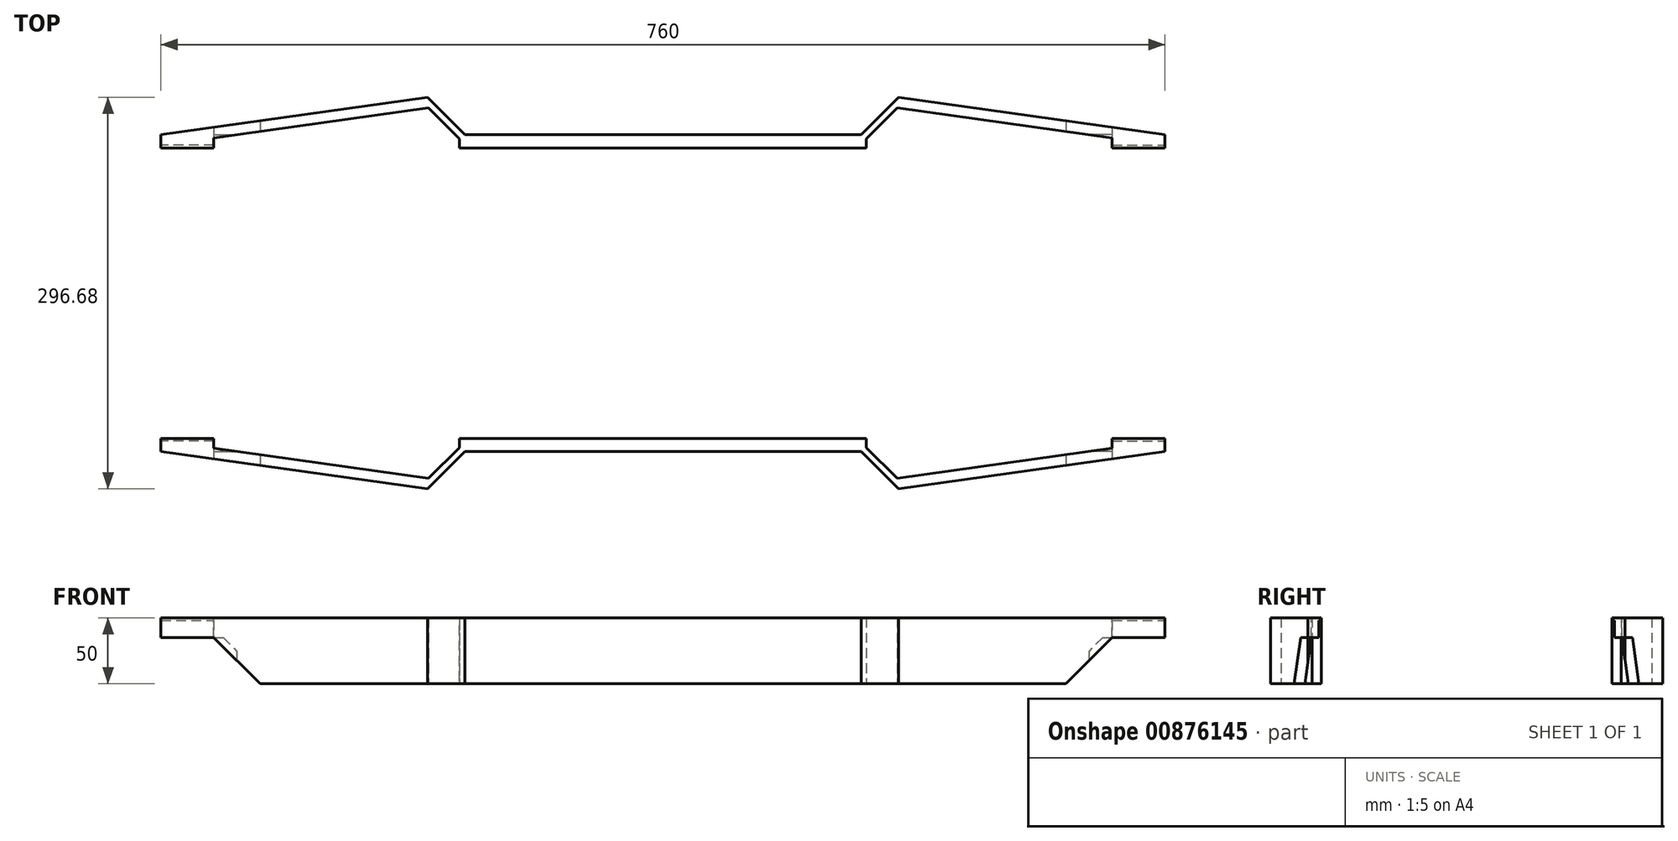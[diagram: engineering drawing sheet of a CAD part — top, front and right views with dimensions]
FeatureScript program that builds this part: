
annotation { "Feature Type Name" : "Feature", "Feature Type Description" : "" }
export const myFeature = defineFeature(function(context is Context, id is Id, definition is map)
    precondition{}
    {
        {
            var Q0;
            Q0=qCreatedBy(makeId("Top.planeOp"),FACE);
            var sketch = newSketch(context, id + "F0", { "sketchPlane" : qUnion([Q0])});
            skLineSegment(sketch, "E0", {"start": v(-380, 120) * mm, "end": v(-380, -120) * mm});
            skLineSegment(sketch, "E1", {"start": v(380, 120) * mm, "end": v(380, -120) * mm});
            skLineSegment(sketch, "E2", {"start": v(150, -120) * mm, "end": v(-150, -120) * mm});
            skLineSegment(sketch, "E3", {"start": v(-150, 120) * mm, "end": v(150, 120) * mm});
            skLineSegment(sketch, "E4", {"start": v(-160, 110) * mm, "end": v(160, 110) * mm, "construction": true});
            skLineSegment(sketch, "E5", {"start": v(160, 110) * mm, "end": v(160, -110) * mm, "construction": true});
            skLineSegment(sketch, "E6", {"start": v(160, -110) * mm, "end": v(-160, -110) * mm, "construction": true});
            skLineSegment(sketch, "E7", {"start": v(-160, -110) * mm, "end": v(-160, 110) * mm, "construction": true});
            skLineSegment(sketch, "E8.0", {"start": v(-150, -110) * mm, "end": v(-150, 110) * mm, "construction": true});
            skLineSegment(sketch, "E9.0", {"start": v(150, 110) * mm, "end": v(150, -110) * mm, "construction": true});
            skLineSegment(sketch, "E10", {"start": v(-150, -110) * mm, "end": v(-150, -120) * mm, "construction": true});
            skLineSegment(sketch, "E11", {"start": v(-150, 110) * mm, "end": v(-150, 120) * mm, "construction": true});
            skLineSegment(sketch, "E12", {"start": v(-150, 120) * mm, "end": v(-178.34, 148.34) * mm});
            skLineSegment(sketch, "E13", {"start": v(-380, 120) * mm, "end": v(-178.34, 148.34) * mm});
            skPoint(sketch, "E14.endSnap0", {"position": v(0, 110) * mm});
            skLineSegment(sketch, "E15.MirrorCS", {"start": v(150, 120) * mm, "end": v(178.34, 148.34) * mm});
            skLineSegment(sketch, "E16.MirrorCS", {"start": v(380, 120) * mm, "end": v(178.34, 148.34) * mm});
            skLineSegment(sketch, "E17.MirrorCS", {"start": v(-150, -120) * mm, "end": v(-178.34, -148.34) * mm, "construction": true});
            skLineSegment(sketch, "E18.MirrorCS", {"start": v(-380, -120) * mm, "end": v(-178.34, -148.34) * mm});
            skLineSegment(sketch, "E19.MirrorCS", {"start": v(150, -120) * mm, "end": v(178.34, -148.34) * mm});
            skLineSegment(sketch, "E20.MirrorCS", {"start": v(-150, -120) * mm, "end": v(-178.34, -148.34) * mm});
            skLineSegment(sketch, "E21.MirrorCS", {"start": v(380, -120) * mm, "end": v(178.34, -148.34) * mm});
            skSolve(sketch);
        }
        {
            var Q0;
            Q0=makeQuery(id+"F0.imprint","IMPRINT",FACE,{"disambiguationData":[TD([[makeQuery(id+"F0.imprint","IMPRINT",EDGE,{"derivedFrom":sQuery(id+"F0.wireOp",EDGE,"E0")}),1.0]])]});
            extrude(context, id + "F1", {"entities" : qUnion([Q0]), "depth" : 50 * mm, "offsetDistance" : 25 * mm});
        }
        {
            var Q0;
            Q0=makeQuery(id+"F1.opExtrude","SWEPT_FACE",FACE,{"disambiguationData":[OSD([sQuery(id+"F0.wireOp",EDGE,"E2")])]});
            var sketch = newSketch(context, id + "F2", { "sketchPlane" : qUnion([Q0])});
            skLineSegment(sketch, "E22", {"start": v(-380, 35) * mm, "end": v(-340, 35) * mm});
            skLineSegment(sketch, "E23", {"start": v(-340, 35) * mm, "end": v(-305, 0) * mm});
            skLineSegment(sketch, "E24", {"start": v(-380, 35) * mm, "end": v(-380, 0) * mm});
            skLineSegment(sketch, "E25", {"start": v(-380, 0) * mm, "end": v(-305, 0) * mm});
            skLineSegment(sketch, "E26.MirrorCS", {"start": v(380, 0) * mm, "end": v(305, 0) * mm});
            skLineSegment(sketch, "E27.MirrorCS", {"start": v(380, 35) * mm, "end": v(380, 0) * mm});
            skLineSegment(sketch, "E28.MirrorCS", {"start": v(380, 35) * mm, "end": v(340, 35) * mm});
            skLineSegment(sketch, "E29.MirrorCS", {"start": v(340, 35) * mm, "end": v(305, 0) * mm});
            skSolve(sketch);
        }
        {
            var Q0;
            Q0=makeQuery(id+"F1.opExtrude","SWEPT_FACE",FACE,{"disambiguationData":[OSD([sQuery(id+"F0.wireOp",EDGE,"E0")])]});
            var sketch = newSketch(context, id + "F3", { "sketchPlane" : qUnion([Q0])});
            skLineSegment(sketch, "E30.0", {"start": v(-110, 45) * mm, "end": v(110, 45) * mm});
            skLineSegment(sketch, "E31.0", {"start": v(-110, 5) * mm, "end": v(110, 5) * mm});
            skLineSegment(sketch, "E32.0", {"start": v(-110, 5) * mm, "end": v(-110, 45) * mm});
            skLineSegment(sketch, "E33.0", {"start": v(110, 45) * mm, "end": v(110, 5) * mm});
            skSolve(sketch);
        }
        {
            var Q0;
            Q0=makeQuery(id+"F3.imprint","IMPRINT",FACE,{"disambiguationData":[TD([[makeQuery(id+"F3.imprint","IMPRINT",EDGE,{"derivedFrom":sQuery(id+"F3.wireOp",EDGE,"E30.0")}),-1.0]])]});
            extrude(context, id + "F4", {"entities" : qUnion([Q0]), "operationType" : NewBodyOperationType.REMOVE, "oppositeDirection" : true, "depth" : 760 * mm, "offsetDistance" : 25 * mm});
        }
        {
            var Q0;
            Q0=makeQuery(id+"F2.imprint","IMPRINT",FACE,{"disambiguationData":[TD([[makeQuery(id+"F2.imprint","IMPRINT",EDGE,{"derivedFrom":sQuery(id+"F2.wireOp",EDGE,"E26.MirrorCS")}),-1.0]])]});
            var Q1;
            Q1=makeQuery(id+"F2.imprint","IMPRINT",FACE,{"disambiguationData":[TD([[makeQuery(id+"F2.imprint","IMPRINT",EDGE,{"derivedFrom":sQuery(id+"F2.wireOp",EDGE,"E22")}),-1.0]])]});
            extrude(context, id + "F5", {"entities" : qUnion([Q0, Q1]), "operationType" : NewBodyOperationType.REMOVE, "oppositeDirection" : true, "depth" : 240 * mm, "offsetDistance" : 25 * mm});
        }
        {
            var Q0;
            Q0=makeQuery(id+"F1.opExtrude","CAP_FACE",FACE,{"disambiguationData":[OSD([sQuery(id+"F0.wireOp",EDGE,"E0"),sQuery(id+"F0.wireOp",EDGE,"E1"),sQuery(id+"F0.wireOp",EDGE,"E2"),sQuery(id+"F0.wireOp",EDGE,"E3")])],"isStart":false});
            var sketch = newSketch(context, id + "F6", { "sketchPlane" : qUnion([Q0])});
            skLineSegment(sketch, "E34", {"start": v(-140, 90) * mm, "end": v(140, 90) * mm});
            skLineSegment(sketch, "E35", {"start": v(140, 90) * mm, "end": v(140, -90) * mm});
            skLineSegment(sketch, "E36", {"start": v(140, -90) * mm, "end": v(-140, -90) * mm});
            skLineSegment(sketch, "E37", {"start": v(-140, -90) * mm, "end": v(-140, 90) * mm});
            skLineSegment(sketch, "E38", {"start": v(160, 110) * mm, "end": v(160, -110) * mm});
            skLineSegment(sketch, "E39", {"start": v(-160, 110) * mm, "end": v(-160, -110) * mm});
            skLineSegment(sketch, "E40", {"start": v(-160, 110) * mm, "end": v(160, 110) * mm});
            skLineSegment(sketch, "E41", {"start": v(160, -110) * mm, "end": v(-160, -110) * mm});
            skSolve(sketch);
        }
        {
            var Q0;
            Q0=qSketchRegion(id+"F6",true);
            extrude(context, id + "F7", {"entities" : qUnion([Q0]), "operationType" : NewBodyOperationType.REMOVE, "oppositeDirection" : true, "depth" : 50 * mm, "offsetDistance" : 25 * mm});
        }
        {
            var Q0;
            Q0=qSketchRegion(id+"F2",true);
            extrude(context, id + "F8", {"entities" : qUnion([Q0]), "operationType" : NewBodyOperationType.REMOVE, "endBound" : BoundingType.SYMMETRIC, "oppositeDirection" : true, "depth" : 871.86 * mm, "offsetDistance" : 25 * mm});
        }
        {
            var Q0;
            {var subQ0=sQuery(id+"F0.wireOp",EDGE,"E18.MirrorCS");var subQ1=sQuery(id+"F0.wireOp",EDGE,"E16.MirrorCS");var subQ2=sQuery(id+"F0.wireOp",EDGE,"E15.MirrorCS");var subQ3=sQuery(id+"F0.wireOp",EDGE,"E13");var subQ4=sQuery(id+"F0.wireOp",EDGE,"E12");var subQ5=sQuery(id+"F0.wireOp",EDGE,"E19.MirrorCS");var subQ6=sQuery(id+"F0.wireOp",EDGE,"E0");var subQ7=sQuery(id+"F0.wireOp",EDGE,"E3");var subQ8=sQuery(id+"F0.wireOp",EDGE,"E1");var subQ9=sQuery(id+"F0.wireOp",EDGE,"E2");var subQ10=sQuery(id+"F0.wireOp",EDGE,"E20.MirrorCS");var subQ11=sQuery(id+"F0.wireOp",EDGE,"E21.MirrorCS");Q0=makeQuery(id+"F7.boolean.opBoolean","SPLIT",FACE,{"disambiguationData":[TD([makeQuery(id+"F1.opExtrude","SWEPT_FACE",FACE,{"disambiguationData":[OSD([subQ6])]})])],"derivedFrom":makeQuery(id+"F1.opExtrude","CAP_FACE",FACE,{"disambiguationData":[OSD([subQ6,subQ8,subQ9,subQ7,subQ4,subQ3,subQ2,subQ1,subQ0,subQ5,subQ10,subQ11])],"isStart":false})});}
            var sketch = newSketch(context, id + "F9", { "sketchPlane" : qUnion([Q0])});
            skLineSegment(sketch, "E42", {"start": v(-165, -110) * mm, "end": v(-305, -110) * mm});
            skLineSegment(sketch, "E43", {"start": v(-305, -110) * mm, "end": v(-305, 110) * mm});
            skLineSegment(sketch, "E44", {"start": v(-305, 110) * mm, "end": v(-165, 110) * mm});
            skLineSegment(sketch, "E45.0", {"start": v(-165, 110) * mm, "end": v(-165, -110) * mm});
            skLineSegment(sketch, "E46", {"start": v(0, 0) * mm, "end": v(0, 58.76) * mm});
            skLineSegment(sketch, "E47.MirrorCS", {"start": v(165, 110) * mm, "end": v(165, -110) * mm});
            skLineSegment(sketch, "E48.MirrorCS", {"start": v(165, -110) * mm, "end": v(305, -110) * mm});
            skLineSegment(sketch, "E49.MirrorCS", {"start": v(305, -110) * mm, "end": v(305, 110) * mm});
            skLineSegment(sketch, "E50.MirrorCS", {"start": v(305, 110) * mm, "end": v(165, 110) * mm});
            skSolve(sketch);
        }
        {
            var Q0;
            Q0=makeQuery(id+"F9.imprint","IMPRINT",FACE,{"disambiguationData":[TD([[makeQuery(id+"F9.imprint","IMPRINT",EDGE,{"derivedFrom":sQuery(id+"F9.wireOp",EDGE,"E42")}),-1.0]])]});
            var Q1;
            Q1=makeQuery(id+"F9.imprint","IMPRINT",FACE,{"disambiguationData":[TD([[makeQuery(id+"F9.imprint","IMPRINT",EDGE,{"derivedFrom":sQuery(id+"F9.wireOp",EDGE,"E47.MirrorCS")}),1.0]])]});
            extrude(context, id + "F10", {"entities" : qUnion([Q0, Q1]), "operationType" : NewBodyOperationType.REMOVE, "oppositeDirection" : true, "depth" : 10 * mm, "offsetDistance" : 25 * mm});
        }
        {
            var Q0;
            Q0=makeQuery(id+"F1.opExtrude","SWEPT_FACE",FACE,{"disambiguationData":[OSD([sQuery(id+"F0.wireOp",EDGE,"E2")])]});
            var sketch = newSketch(context, id + "F11", { "sketchPlane" : qUnion([Q0])});
            skLineSegment(sketch, "E51", {"start": v(-305, 50) * mm, "end": v(-305, 0) * mm});
            skLineSegment(sketch, "E52", {"start": v(-340, 50) * mm, "end": v(-340, 35) * mm});
            skLineSegment(sketch, "E53", {"start": v(-340, 35) * mm, "end": v(-305, 0) * mm});
            skLineSegment(sketch, "E54.0", {"start": v(-332.93, 35) * mm, "end": v(-305, 7.07) * mm});
            skLineSegment(sketch, "E55", {"start": v(-340, 35) * mm, "end": v(-332.93, 35) * mm});
            skLineSegment(sketch, "E56", {"start": v(0, 0) * mm, "end": v(0, 50) * mm});
            skLineSegment(sketch, "E57", {"start": v(-340, 35) * mm, "end": v(-346.55, 35) * mm});
            skLineSegment(sketch, "E58.MirrorCS", {"start": v(332.93, 35) * mm, "end": v(305, 7.07) * mm});
            skLineSegment(sketch, "E59.MirrorCS", {"start": v(340, 35) * mm, "end": v(305, 0) * mm});
            skLineSegment(sketch, "E60.MirrorCS", {"start": v(340, 35) * mm, "end": v(332.93, 35) * mm});
            skLineSegment(sketch, "E61", {"start": v(305, 7.07) * mm, "end": v(305, 0) * mm});
            skSolve(sketch);
        }
        {
            var Q0;
            {var subQ0=sQuery(id+"F11.wireOp",EDGE,"E53");Q0=makeQuery(id+"F11.imprint","IMPRINT",FACE,{"disambiguationData":[TD([[makeQuery(id+"F11.imprint","IMPRINT",EDGE,{"derivedFrom":subQ0}),1.0]])]});}
            var Q1;
            Q1=makeQuery(id+"F11.imprint","IMPRINT",FACE,{"disambiguationData":[TD([[makeQuery(id+"F11.imprint","IMPRINT",EDGE,{"derivedFrom":sQuery(id+"F11.wireOp",EDGE,"E58.MirrorCS")}),1.0]])]});
            extrude(context, id + "F12", {"entities" : qUnion([Q0, Q1]), "oppositeDirection" : true, "depth" : 240 * mm, "offsetDistance" : 25 * mm});
        }
        {
            var Q0;
            Q0=makeQuery(id+"F7.boolean.opBoolean","SPLIT",FACE,{"disambiguationData":[TD([makeQuery(id+"F7.opExtrude","SWEPT_FACE",FACE,{"disambiguationData":[OSD([sQuery(id+"F6.wireOp",EDGE,"E34")])]})])],"derivedFrom":makeQuery(id+"F1.opExtrude","CAP_FACE",FACE,{"disambiguationData":[OSD([sQuery(id+"F0.wireOp",EDGE,"E0"),sQuery(id+"F0.wireOp",EDGE,"E1"),sQuery(id+"F0.wireOp",EDGE,"E2"),sQuery(id+"F0.wireOp",EDGE,"E3"),sQuery(id+"F0.wireOp",EDGE,"E12"),sQuery(id+"F0.wireOp",EDGE,"E13"),sQuery(id+"F0.wireOp",EDGE,"E15.MirrorCS"),sQuery(id+"F0.wireOp",EDGE,"E16.MirrorCS"),sQuery(id+"F0.wireOp",EDGE,"E18.MirrorCS"),sQuery(id+"F0.wireOp",EDGE,"E19.MirrorCS"),sQuery(id+"F0.wireOp",EDGE,"E20.MirrorCS"),sQuery(id+"F0.wireOp",EDGE,"E21.MirrorCS")])],"isStart":false})});
            extrude(context, id + "F13", {"entities" : qUnion([Q0]), "operationType" : NewBodyOperationType.REMOVE, "oppositeDirection" : true, "depth" : 25 * mm, "offsetDistance" : 25 * mm});
        }
        {
            var Q0;
            Q0=makeQuery(id+"F7.boolean.opBoolean","SPLIT",FACE,{"disambiguationData":[TD([makeQuery(id+"F7.opExtrude","SWEPT_FACE",FACE,{"disambiguationData":[OSD([sQuery(id+"F6.wireOp",EDGE,"E34")])]})])],"derivedFrom":makeQuery(id+"F1.opExtrude","CAP_FACE",FACE,{"disambiguationData":[OSD([sQuery(id+"F0.wireOp",EDGE,"E0"),sQuery(id+"F0.wireOp",EDGE,"E1"),sQuery(id+"F0.wireOp",EDGE,"E2"),sQuery(id+"F0.wireOp",EDGE,"E3"),sQuery(id+"F0.wireOp",EDGE,"E12"),sQuery(id+"F0.wireOp",EDGE,"E13"),sQuery(id+"F0.wireOp",EDGE,"E15.MirrorCS"),sQuery(id+"F0.wireOp",EDGE,"E16.MirrorCS"),sQuery(id+"F0.wireOp",EDGE,"E18.MirrorCS"),sQuery(id+"F0.wireOp",EDGE,"E19.MirrorCS"),sQuery(id+"F0.wireOp",EDGE,"E20.MirrorCS"),sQuery(id+"F0.wireOp",EDGE,"E21.MirrorCS")])],"isStart":true})});
            extrude(context, id + "F14", {"entities" : qUnion([Q0]), "operationType" : NewBodyOperationType.REMOVE, "oppositeDirection" : true, "depth" : 25 * mm, "offsetDistance" : 25 * mm});
        }
        {
            var Q0;
            Q0=makeQuery(id+"F7.boolean.opBoolean","COPY",FACE,{"disambiguationData":[TD([makeQuery(id+"F4.boolean.opBoolean","COPY",FACE,{"derivedFrom":makeQuery(id+"F4.opExtrude","SWEPT_FACE",FACE,{"disambiguationData":[OSD([sQuery(id+"F3.wireOp",EDGE,"E30.0")])]})})])],"derivedFrom":makeQuery(id+"F7.opExtrude","SWEPT_FACE",FACE,{"disambiguationData":[OSD([sQuery(id+"F6.wireOp",EDGE,"E38")])]})});
            var sketch = newSketch(context, id + "F15", { "sketchPlane" : qUnion([Q0])});
            skLineSegment(sketch, "E62", {"start": v(-110, 45) * mm, "end": v(-110, 5) * mm});
            skLineSegment(sketch, "E63", {"start": v(-110, 45) * mm, "end": v(110, 45) * mm});
            skLineSegment(sketch, "E64", {"start": v(110, 45) * mm, "end": v(110, 5) * mm});
            skLineSegment(sketch, "E65", {"start": v(-110, 5) * mm, "end": v(110, 5) * mm});
            skSolve(sketch);
        }
        {
            var Q0;
            Q0=makeQuery(id+"F7.boolean.opBoolean","COPY",FACE,{"disambiguationData":[TD([makeQuery(id+"F4.boolean.opBoolean","COPY",FACE,{"derivedFrom":makeQuery(id+"F4.opExtrude","SWEPT_FACE",FACE,{"disambiguationData":[OSD([sQuery(id+"F3.wireOp",EDGE,"E31.0")])]})})])],"derivedFrom":makeQuery(id+"F7.opExtrude","SWEPT_FACE",FACE,{"disambiguationData":[OSD([sQuery(id+"F6.wireOp",EDGE,"E39")])]})});
            var sketch = newSketch(context, id + "F16", { "sketchPlane" : qUnion([Q0])});
            skLineSegment(sketch, "E66", {"start": v(-110, 5) * mm, "end": v(-110, 45) * mm});
            skLineSegment(sketch, "E67", {"start": v(-110, 5) * mm, "end": v(110, 5) * mm});
            skLineSegment(sketch, "E68", {"start": v(110, 5) * mm, "end": v(110, 45) * mm});
            skLineSegment(sketch, "E69", {"start": v(-110, 45) * mm, "end": v(110, 45) * mm});
            skSolve(sketch);
        }
        {
            var Q0;
            Q0=qSketchRegion(id+"F16",true);
            extrude(context, id + "F17", {"entities" : qUnion([Q0]), "operationType" : NewBodyOperationType.ADD, "oppositeDirection" : true, "depth" : 5 * mm, "offsetDistance" : 25 * mm});
        }
        {
            var Q0;
            Q0=makeQuery(id+"F15.imprint","IMPRINT",FACE,{"disambiguationData":[TD([[makeQuery(id+"F15.imprint","IMPRINT",EDGE,{"derivedFrom":sQuery(id+"F15.wireOp",EDGE,"E62")}),1.0]])]});
            extrude(context, id + "F18", {"entities" : qUnion([Q0]), "operationType" : NewBodyOperationType.ADD, "oppositeDirection" : true, "depth" : 5 * mm, "offsetDistance" : 25 * mm});
        }
        {
            var Q0;
            Q0=makeQuery(id+"F10.boolean.opBoolean","COPY",FACE,{"derivedFrom":makeQuery(id+"F10.opExtrude","SWEPT_FACE",FACE,{"disambiguationData":[OSD([sQuery(id+"F9.wireOp",EDGE,"E43")])]})});
            extrude(context, id + "F19", {"entities" : qUnion([Q0]), "operationType" : NewBodyOperationType.REMOVE, "oppositeDirection" : true, "depth" : 121.6 * mm, "offsetDistance" : 25 * mm});
        }
        {
            var Q0;
            Q0=makeQuery(id+"F10.boolean.opBoolean","COPY",FACE,{"derivedFrom":makeQuery(id+"F10.opExtrude","SWEPT_FACE",FACE,{"disambiguationData":[OSD([sQuery(id+"F9.wireOp",EDGE,"E49.MirrorCS")])]})});
            extrude(context, id + "F20", {"entities" : qUnion([Q0]), "operationType" : NewBodyOperationType.REMOVE, "endBound" : BoundingType.SYMMETRIC, "depth" : 2865.48 * mm, "offsetDistance" : 25 * mm});
        }
        {
            var Q0;
            Q0=makeQuery(id+"F17.boolean.opBoolean","MERGE",FACE,{"derivedFrom":[makeQuery(id+"F10.boolean.opBoolean","COPY",FACE,{"derivedFrom":makeQuery(id+"F10.opExtrude","SWEPT_FACE",FACE,{"disambiguationData":[OSD([sQuery(id+"F9.wireOp",EDGE,"E45.0")])]})}),makeQuery(id+"F17.opExtrude","CAP_FACE",FACE,{"disambiguationData":[OSD([sQuery(id+"F16.wireOp",EDGE,"E66"),sQuery(id+"F16.wireOp",EDGE,"E67"),sQuery(id+"F16.wireOp",EDGE,"E68"),sQuery(id+"F16.wireOp",EDGE,"E69")])],"isStart":false})]});
            extrude(context, id + "F21", {"entities" : qUnion([Q0]), "operationType" : NewBodyOperationType.REMOVE, "endBound" : BoundingType.SYMMETRIC, "oppositeDirection" : true, "depth" : 1589.2 * mm, "offsetDistance" : 25 * mm});
        }
        {
            var Q0;
            {var subQ16=makeQuery(id+"F7.opExtrude","SWEPT_FACE",FACE,{"disambiguationData":[OSD([sQuery(id+"F6.wireOp",EDGE,"E39")])]});Q0=makeQuery(id+"F17.boolean.opBoolean","MERGE",FACE,{"derivedFrom":[makeQuery(id+"F7.boolean.opBoolean","COPY",FACE,{"disambiguationData":[TD([makeQuery(id+"F4.boolean.opBoolean","COPY",FACE,{"derivedFrom":makeQuery(id+"F4.opExtrude","SWEPT_FACE",FACE,{"disambiguationData":[OSD([sQuery(id+"F3.wireOp",EDGE,"E30.0")])]})})])],"derivedFrom":subQ16}),makeQuery(id+"F7.boolean.opBoolean","COPY",FACE,{"disambiguationData":[TD([makeQuery(id+"F4.boolean.opBoolean","COPY",FACE,{"derivedFrom":makeQuery(id+"F4.opExtrude","SWEPT_FACE",FACE,{"disambiguationData":[OSD([sQuery(id+"F3.wireOp",EDGE,"E31.0")])]})})])],"derivedFrom":subQ16}),makeQuery(id+"F17.opExtrude","CAP_FACE",FACE,{"disambiguationData":[OSD([sQuery(id+"F16.wireOp",EDGE,"E66"),sQuery(id+"F16.wireOp",EDGE,"E67"),sQuery(id+"F16.wireOp",EDGE,"E68"),sQuery(id+"F16.wireOp",EDGE,"E69")])],"isStart":true})]});}
            extrude(context, id + "F22", {"entities" : qUnion([Q0]), "operationType" : NewBodyOperationType.REMOVE, "endBound" : BoundingType.SYMMETRIC, "depth" : 1696.6 * mm, "offsetDistance" : 25 * mm});
        }
        {
            var Q0;
            {var subQ1=sQuery(id+"F0.wireOp",EDGE,"E19.MirrorCS");var subQ3=sQuery(id+"F0.wireOp",EDGE,"E21.MirrorCS");var subQ7=sQuery(id+"F0.wireOp",EDGE,"E2");var subQ8=makeQuery(id+"F1.opExtrude","SWEPT_FACE",FACE,{"disambiguationData":[OSD([subQ7])]});var subQ9=sQuery(id+"F0.wireOp",EDGE,"E18.MirrorCS");var subQ13=sQuery(id+"F0.wireOp",EDGE,"E20.MirrorCS");var subQ17=sQuery(id+"F0.wireOp",EDGE,"E16.MirrorCS");var subQ18=sQuery(id+"F0.wireOp",EDGE,"E15.MirrorCS");var subQ22=sQuery(id+"F0.wireOp",EDGE,"E3");var subQ23=sQuery(id+"F0.wireOp",EDGE,"E12");var subQ27=sQuery(id+"F0.wireOp",EDGE,"E13");Q0=makeQuery(id+"F22.boolean.opBoolean","SPLIT",FACE,{"disambiguationData":[TD([subQ8])],"derivedFrom":makeQuery(id+"F7.boolean.opBoolean","SPLIT",FACE,{"disambiguationData":[TD([subQ8])],"derivedFrom":makeQuery(id+"F1.opExtrude","CAP_FACE",FACE,{"disambiguationData":[OSD([sQuery(id+"F0.wireOp",EDGE,"E0"),sQuery(id+"F0.wireOp",EDGE,"E1"),subQ7,subQ22,subQ23,subQ27,subQ18,subQ17,subQ9,subQ1,subQ13,subQ3])],"isStart":true})})});}
            var sketch = newSketch(context, id + "F23", { "sketchPlane" : qUnion([Q0])});
            skLineSegment(sketch, "E70", {"start": v(-301, 110) * mm, "end": v(-154, 110) * mm});
            skLineSegment(sketch, "E71.0", {"start": v(-177.46, 140.39) * mm, "end": v(-301, 123.02) * mm});
            skLineSegment(sketch, "E72.0", {"start": v(-301, 123.02) * mm, "end": v(-301, 110) * mm});
            skLineSegment(sketch, "E73.0", {"start": v(-154, 116.93) * mm, "end": v(-177.46, 140.39) * mm});
            skLineSegment(sketch, "E74.0", {"start": v(-154, 110) * mm, "end": v(-154, 116.93) * mm});
            skLineSegment(sketch, "E75.MirrorCS", {"start": v(-301, -110) * mm, "end": v(-154, -110) * mm});
            skLineSegment(sketch, "E76.MirrorCS", {"start": v(-177.46, -140.39) * mm, "end": v(-301, -123.02) * mm});
            skLineSegment(sketch, "E77.MirrorCS", {"start": v(-301, -123.02) * mm, "end": v(-301, -110) * mm});
            skLineSegment(sketch, "E78.MirrorCS", {"start": v(-154, -116.93) * mm, "end": v(-177.46, -140.39) * mm});
            skLineSegment(sketch, "E79.MirrorCS", {"start": v(-154, -110) * mm, "end": v(-154, -116.93) * mm});
            skLineSegment(sketch, "E80.MirrorCS", {"start": v(154, 116.93) * mm, "end": v(177.46, 140.39) * mm});
            skLineSegment(sketch, "E81.MirrorCS", {"start": v(301, 110) * mm, "end": v(154, 110) * mm});
            skLineSegment(sketch, "E82.MirrorCS", {"start": v(301, -110) * mm, "end": v(154, -110) * mm});
            skLineSegment(sketch, "E83.MirrorCS", {"start": v(154, 110) * mm, "end": v(154, 116.93) * mm});
            skLineSegment(sketch, "E84.MirrorCS", {"start": v(177.46, 140.39) * mm, "end": v(301, 123.02) * mm});
            skLineSegment(sketch, "E85.MirrorCS", {"start": v(301, 123.02) * mm, "end": v(301, 110) * mm});
            skLineSegment(sketch, "E86.MirrorCS", {"start": v(154, -110) * mm, "end": v(154, -116.93) * mm});
            skLineSegment(sketch, "E87.MirrorCS", {"start": v(154, -116.93) * mm, "end": v(177.46, -140.39) * mm});
            skLineSegment(sketch, "E88.MirrorCS", {"start": v(301, -123.02) * mm, "end": v(301, -110) * mm});
            skLineSegment(sketch, "E89.MirrorCS", {"start": v(177.46, -140.39) * mm, "end": v(301, -123.02) * mm});
            skSolve(sketch);
        }
        {
            var Q0;
            Q0=makeQuery(id+"F23.imprint","IMPRINT",FACE,{"disambiguationData":[TD([[makeQuery(id+"F23.imprint","IMPRINT",EDGE,{"derivedFrom":sQuery(id+"F23.wireOp",EDGE,"E75.MirrorCS")}),-1.0]])]});
            var Q1;
            Q1=makeQuery(id+"F23.imprint","IMPRINT",FACE,{"disambiguationData":[TD([[makeQuery(id+"F23.imprint","IMPRINT",EDGE,{"derivedFrom":sQuery(id+"F23.wireOp",EDGE,"E86.MirrorCS")}),1.0]])]});
            extrude(context, id + "F24", {"entities" : qUnion([Q0, Q1]), "operationType" : NewBodyOperationType.REMOVE, "oppositeDirection" : true, "depth" : 50 * mm, "offsetDistance" : 25 * mm});
        }
        {
            var Q0;
            Q0=makeQuery(id+"F23.imprint","IMPRINT",FACE,{"disambiguationData":[TD([[makeQuery(id+"F23.imprint","IMPRINT",EDGE,{"derivedFrom":sQuery(id+"F23.wireOp",EDGE,"E70")}),-1.0]])]});
            var Q1;
            Q1=makeQuery(id+"F23.imprint","IMPRINT",FACE,{"disambiguationData":[TD([[makeQuery(id+"F23.imprint","IMPRINT",EDGE,{"derivedFrom":sQuery(id+"F23.wireOp",EDGE,"E80.MirrorCS")}),-1.0]])]});
            extrude(context, id + "F25", {"entities" : qUnion([Q0, Q1]), "operationType" : NewBodyOperationType.REMOVE, "oppositeDirection" : true, "depth" : 50 * mm, "offsetDistance" : 25 * mm});
        }
        {
            var Q0;
            {var subQ0=sQuery(id+"F0.wireOp",EDGE,"E2");var subQ1=makeQuery(id+"F1.opExtrude","SWEPT_FACE",FACE,{"disambiguationData":[OSD([subQ0])]});var subQ2=sQuery(id+"F0.wireOp",EDGE,"E1");var subQ4=sQuery(id+"F0.wireOp",EDGE,"E18.MirrorCS");var subQ6=sQuery(id+"F0.wireOp",EDGE,"E0");var subQ7=makeQuery(id+"F1.opExtrude","SWEPT_FACE",FACE,{"disambiguationData":[OSD([subQ6])]});var subQ8=sQuery(id+"F0.wireOp",EDGE,"E19.MirrorCS");var subQ10=sQuery(id+"F0.wireOp",EDGE,"E20.MirrorCS");var subQ12=sQuery(id+"F0.wireOp",EDGE,"E21.MirrorCS");var subQ15=sQuery(id+"F0.wireOp",EDGE,"E16.MirrorCS");var subQ16=sQuery(id+"F0.wireOp",EDGE,"E15.MirrorCS");var subQ17=sQuery(id+"F0.wireOp",EDGE,"E13");var subQ18=sQuery(id+"F0.wireOp",EDGE,"E12");var subQ19=sQuery(id+"F0.wireOp",EDGE,"E3");Q0=makeQuery(id+"F20.boolean.opBoolean","SPLIT",FACE,{"disambiguationData":[TD([subQ1])],"derivedFrom":makeQuery(id+"F7.boolean.opBoolean","SPLIT",FACE,{"disambiguationData":[TD([subQ7])],"derivedFrom":makeQuery(id+"F1.opExtrude","CAP_FACE",FACE,{"disambiguationData":[OSD([subQ6,subQ2,subQ0,subQ19,subQ18,subQ17,subQ16,subQ15,subQ4,subQ8,subQ10,subQ12])],"isStart":false})})});}
            var sketch = newSketch(context, id + "F26", { "sketchPlane" : qUnion([Q0])});
            skLineSegment(sketch, "E90.0", {"start": v(301, -123.02) * mm, "end": v(340, -117.54) * mm});
            skLineSegment(sketch, "E91", {"start": v(340, -110) * mm, "end": v(340, -117.54) * mm});
            skLineSegment(sketch, "E92", {"start": v(301, -110) * mm, "end": v(340, -110) * mm});
            skLineSegment(sketch, "E93", {"start": v(301, -110) * mm, "end": v(301, -123.02) * mm});
            skLineSegment(sketch, "E94.MirrorCS", {"start": v(-301, -110) * mm, "end": v(-301, -123.02) * mm});
            skLineSegment(sketch, "E95.MirrorCS", {"start": v(-301, -110) * mm, "end": v(-340, -110) * mm});
            skLineSegment(sketch, "E96.MirrorCS", {"start": v(-340, -110) * mm, "end": v(-340, -117.54) * mm});
            skLineSegment(sketch, "E97.MirrorCS", {"start": v(-301, -123.02) * mm, "end": v(-340, -117.54) * mm});
            skLineSegment(sketch, "E98.MirrorCS", {"start": v(340, 110) * mm, "end": v(340, 117.54) * mm});
            skLineSegment(sketch, "E99.MirrorCS", {"start": v(301, 110) * mm, "end": v(340, 110) * mm});
            skLineSegment(sketch, "E100.MirrorCS", {"start": v(301, 123.02) * mm, "end": v(340, 117.54) * mm});
            skLineSegment(sketch, "E101.MirrorCS", {"start": v(301, 110) * mm, "end": v(301, 123.02) * mm});
            skLineSegment(sketch, "E102.MirrorCS", {"start": v(-301, 110) * mm, "end": v(-301, 123.02) * mm});
            skLineSegment(sketch, "E103.MirrorCS", {"start": v(-301, 110) * mm, "end": v(-340, 110) * mm});
            skLineSegment(sketch, "E104.MirrorCS", {"start": v(-301, 123.02) * mm, "end": v(-340, 117.54) * mm});
            skLineSegment(sketch, "E105.MirrorCS", {"start": v(-340, 110) * mm, "end": v(-340, 117.54) * mm});
            skSolve(sketch);
        }
        {
            var Q0;
            Q0 = qSketchRegion(id + "F26", true);
            extrude(context, id + "F27", {"entities" : qUnion([Q0]), "operationType" : NewBodyOperationType.REMOVE, "oppositeDirection" : true, "depth" : 50 * mm, "offsetDistance" : 25 * mm});
        }
        {
            var Q0;
            Q0=makeQuery(id+"F25.boolean.opBoolean","COPY",FACE,{"derivedFrom":makeQuery(id+"F25.opExtrude","SWEPT_FACE",FACE,{"disambiguationData":[OSD([sQuery(id+"F23.wireOp",EDGE,"E83.MirrorCS")])]})});
            var sketch = newSketch(context, id + "F28", { "sketchPlane" : qUnion([Q0])});
            skLineSegment(sketch, "E106", {"start": v(-110, 48) * mm, "end": v(-110, 2) * mm});
            skLineSegment(sketch, "E107.0", {"start": v(-110, 2) * mm, "end": v(-112, 2) * mm});
            skLineSegment(sketch, "E108.0", {"start": v(-112, 48) * mm, "end": v(-110, 48) * mm});
            skLineSegment(sketch, "E109.0", {"start": v(-112, 48) * mm, "end": v(-112, 2) * mm});
            skLineSegment(sketch, "E110.MirrorCS", {"start": v(110, 2) * mm, "end": v(112, 2) * mm});
            skLineSegment(sketch, "E111.MirrorCS", {"start": v(110, 48) * mm, "end": v(110, 2) * mm});
            skLineSegment(sketch, "E112.MirrorCS", {"start": v(112, 48) * mm, "end": v(112, 2) * mm});
            skLineSegment(sketch, "E113.MirrorCS", {"start": v(112, 48) * mm, "end": v(110, 48) * mm});
            skSolve(sketch);
        }
        {
            var Q0;
            Q0=makeQuery(id+"F28.imprint","IMPRINT",FACE,{"disambiguationData":[TD([[makeQuery(id+"F28.imprint","IMPRINT",EDGE,{"derivedFrom":sQuery(id+"F28.wireOp",EDGE,"E106")}),-1.0]])]});
            var Q1;
            Q1=makeQuery(id+"F28.imprint","IMPRINT",FACE,{"disambiguationData":[TD([[makeQuery(id+"F28.imprint","IMPRINT",EDGE,{"derivedFrom":sQuery(id+"F28.wireOp",EDGE,"E110.MirrorCS")}),1.0]])]});
            extrude(context, id + "F29", {"entities" : qUnion([Q0, Q1]), "operationType" : NewBodyOperationType.REMOVE, "endBound" : BoundingType.SYMMETRIC, "oppositeDirection" : true, "depth" : 1554.04 * mm, "offsetDistance" : 25 * mm});
        }
        {
            var Q0;
            Q0=makeQuery(id+"F28.imprint","IMPRINT",FACE,{"disambiguationData":[TD([[makeQuery(id+"F28.imprint","IMPRINT",EDGE,{"derivedFrom":sQuery(id+"F28.wireOp",EDGE,"E106")}),-1.0]])]});
            var Q1;
            Q1=makeQuery(id+"F28.imprint","IMPRINT",FACE,{"disambiguationData":[TD([[makeQuery(id+"F28.imprint","IMPRINT",EDGE,{"derivedFrom":sQuery(id+"F28.wireOp",EDGE,"E110.MirrorCS")}),1.0]])]});
            extrude(context, id + "F30", {"entities" : qUnion([Q0, Q1]), "operationType" : NewBodyOperationType.ADD, "oppositeDirection" : true, "depth" : 308 * mm, "offsetDistance" : 25 * mm});
        }
    });
